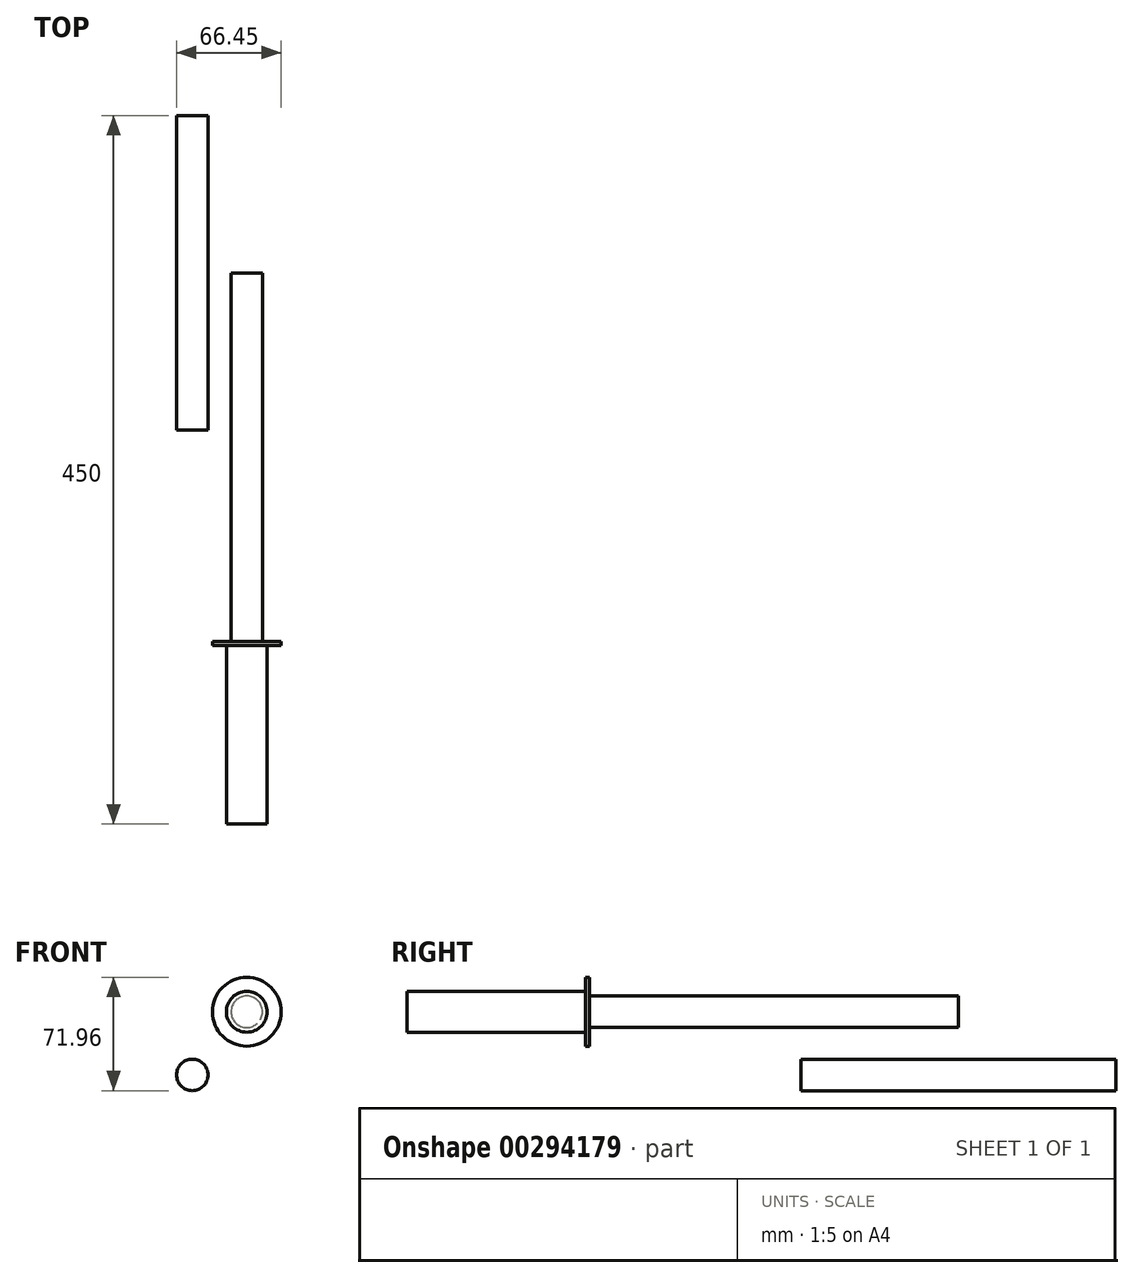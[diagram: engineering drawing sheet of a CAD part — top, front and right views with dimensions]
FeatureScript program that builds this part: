
annotation { "Feature Type Name" : "Feature", "Feature Type Description" : "" }
export const myFeature = defineFeature(function(context is Context, id is Id, definition is map)
    precondition{}
    {
        {
            var Q0;
            Q0=qCreatedBy(makeId("Front.planeOp"),FACE);
            var sketch = newSketch(context, id + "F0", { "sketchPlane" : qUnion([Q0])});
            skCircle(sketch, "E0", {"center": v(0, 0) * mm, "radius": 10 * mm});
            skSolve(sketch);
        }
        {
            var Q0;
            Q0 = qSketchRegion(id + "F0", true);
            extrude(context, id + "F1", {"entities" : qUnion([Q0]), "endBound" : BoundingType.SYMMETRIC, "depth" : 200 * mm});
        }
        {
            var Q0;
            Q0=qCreatedBy(makeId("Front.planeOp"),FACE);
            var sketch = newSketch(context, id + "F2", { "sketchPlane" : qUnion([Q0])});
            skCircle(sketch, "E1", {"center": v(34.6, 40.1) * mm, "radius": 10 * mm});
            skSolve(sketch);
        }
        {
            var Q0;
            Q0 = qSketchRegion(id + "F2", true);
            extrude(context, id + "F3", {"entities" : qUnion([Q0]), "depth" : 350 * mm});
        }
        {
            var Q0;
            Q0=makeQuery(id+"F3.opExtrude","CAP_FACE",FACE,{"disambiguationData":[OSD([sQuery(id+"F2.wireOp",EDGE,"E1")])],"isStart":false});
            var sketch = newSketch(context, id + "F4", { "sketchPlane" : qUnion([Q0])});
            skCircle(sketch, "E2", {"center": v(34.6, 40.1) * mm, "radius": 12.96 * mm});
            skSolve(sketch);
        }
        {
            var Q0;
            Q0 = qSketchRegion(id + "F4", true);
            extrude(context, id + "F5", {"entities" : qUnion([Q0]), "operationType" : NewBodyOperationType.ADD, "oppositeDirection" : true, "depth" : 113.28 * mm});
        }
        {
            var Q0;
            Q0=makeQuery(id+"F5.opExtrude","CAP_FACE",FACE,{"disambiguationData":[OSD([sQuery(id+"F4.wireOp",EDGE,"E2")])],"isStart":false});
            var sketch = newSketch(context, id + "F6", { "sketchPlane" : qUnion([Q0])});
            skCircle(sketch, "E3", {"center": v(-34.6, 40.1) * mm, "radius": 21.85 * mm});
            skSolve(sketch);
        }
        {
            var Q0;
            Q0 = qSketchRegion(id + "F6", true);
            extrude(context, id + "F7", {"entities" : qUnion([Q0]), "operationType" : NewBodyOperationType.ADD, "depth" : 2.54 * mm});
        }
    });
